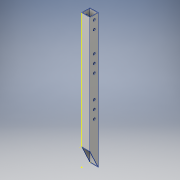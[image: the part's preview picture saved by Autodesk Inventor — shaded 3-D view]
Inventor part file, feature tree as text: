
AUTODESK INVENTOR PART (.ipt)
format: ipt  version: 2016 (Build 200138000, 138)  size: 157,696 bytes
history: native  units: in
note: dims shown in document units (in); Inventor stores cm internally (conversion verified against a paired STEP export)
features: sketch x5, extrude x4
ambient origin geometry x8: Origin, YZ Plane, XZ Plane, XY Plane, X Axis, Y Axis, Z Axis, Center Point
bodies: Solid1 (feature_tree)
feature tree (9):
  extrude  "Extrusion1"  Depth=1.0in
  extrude  "Extrusion2"  Depth=0.0625in TaperAngle=0.0deg
  extrude  "Extrusion3"  Depth=1.0in TaperAngle=0.0deg
  extrude  "Extrusion4"  Depth=0.5in
  sketch  "Sketch5"  dims[d10=0.5in d11=0.2656in d12=0.5in d13=1.5in d14=1.0in d15=0.0in d16=0.2656in d17=6.0in d18=0.2656in d19=1.0in d20=0.2656in d21=0.5in d22=0.5in d23=0.5in d24=1.0in d25=0.2656in d26=1.0in d27=1.0in d28=0.5in d30=10.75in d31=1.0in d32=0.0in]
  sketch  "Sketch1"  dims[d0=1.0in d1=1.0in]
  sketch  "Sketch2"  dims[d2=0.0625in d3=16.0in d4=0.0in]
  sketch  "Sketch3"  dims[d5=0.1718in d6=1.0in d7=0.0in]
  sketch  "Sketch4"  dims[d8=0.2656in d9=0.5in]
